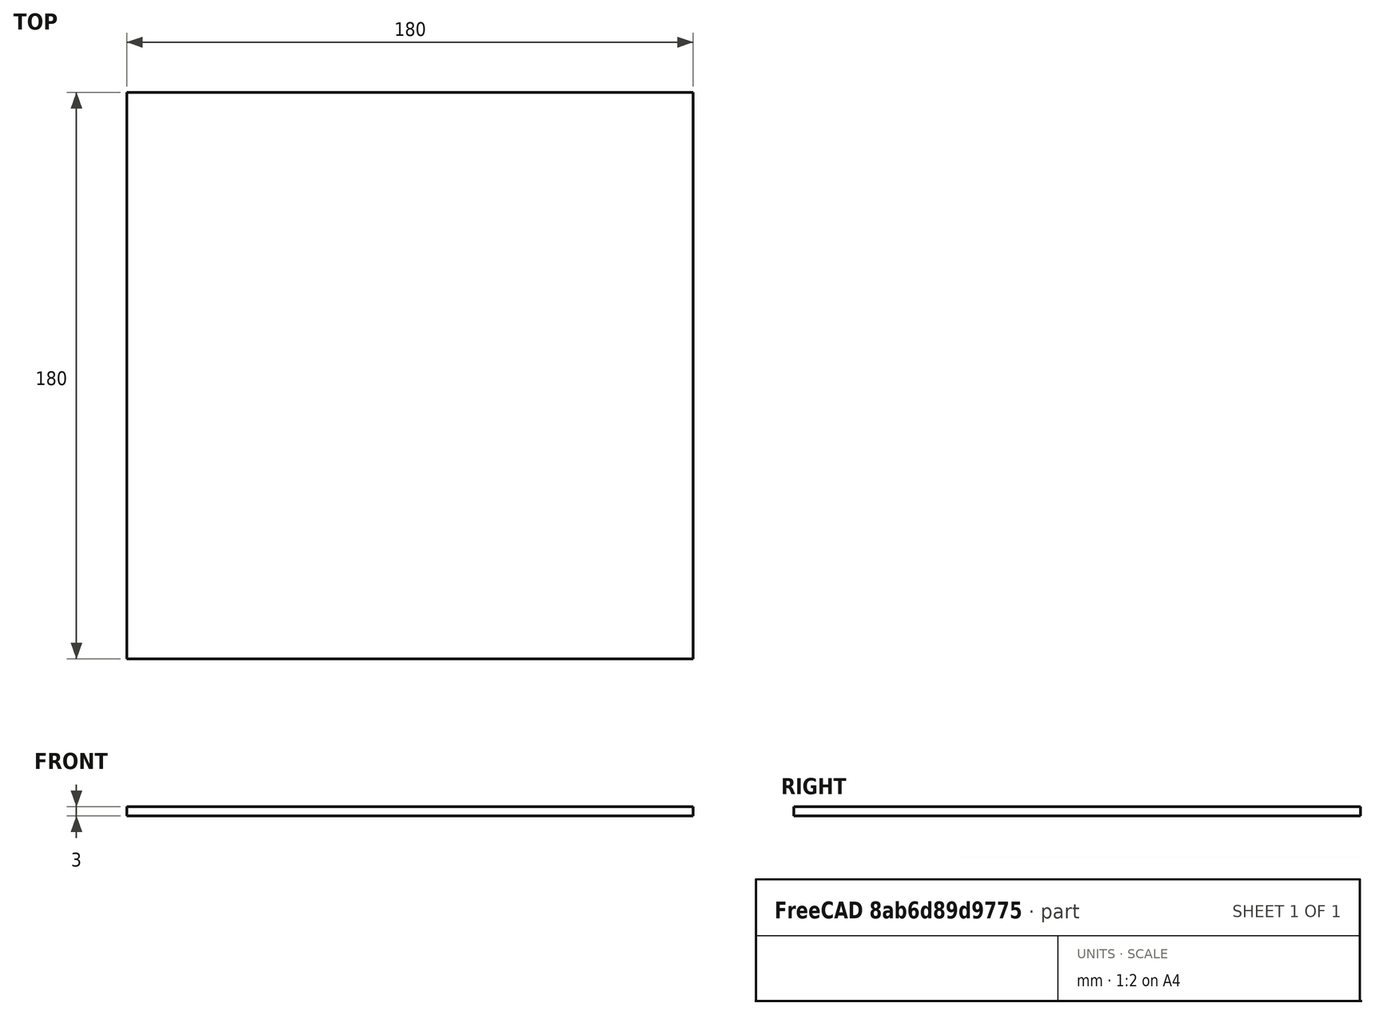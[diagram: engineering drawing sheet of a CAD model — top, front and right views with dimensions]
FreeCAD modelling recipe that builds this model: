
FCSTD DOCUMENT  (FreeCAD 0.19R24276 (Git))
Label: PB3D_TriPlate_Ground
License: All rights reserved
LicenseURL: http://en.wikipedia.org/wiki/All_rights_reserved
objects: Sketcher::SketchObject×1, PartDesign::Pad×1, PartDesign::Body×1, App::Part×1
note: 4 computed .brp shape members not serialized (recipe doc carries the construction recipe); baked Part::Feature solids carry a one-line shape summary decoded from their .brp

FEATURE [Sketcher::SketchObject] Sketch
  FullyConstrained = true
  MapMode = 5
  Support = -> [XY_Plane001]
  sketch-geometry (4):
    g0: LineSegment StartX=-90 StartY=90 StartZ=0 EndX=90 EndY=90 EndZ=0
    g1: LineSegment StartX=90 StartY=90 StartZ=0 EndX=90 EndY=-90 EndZ=0
    g2: LineSegment StartX=90 StartY=-90 StartZ=0 EndX=-90 EndY=-90 EndZ=0
    g3: LineSegment StartX=-90 StartY=-90 StartZ=0 EndX=-90 EndY=90 EndZ=0
  constraints (11):
    c: Coincident(g0,g1)
    c: Coincident(g1,g2)
    c: Coincident(g2,g3)
    c: Coincident(g3,g0)
    c: Horizontal(g0)
    c: Horizontal(g2)
    c: Vertical(g1)
    c: Vertical(g3)
    c: Symmetric(g0,g2,g-1)
    c: Equal(g1,g0)
    c: Distance(g1) = 180
FEATURE [PartDesign::Pad] Pad
  Direction = (1,1,1)
  Length = 3
  Length2 = 100
  Profile = -> Sketch
  Reversed = true
  Type = 0
FEATURE [PartDesign::Body] Body  label="Ground"
  Group = -> [Sketch,Pad]
  Origin = -> Origin001
  Tip = -> Pad
FEATURE [App::Part] Part  label="TriplateGroundPart"
  Group = -> [Body]
  Origin = -> Origin
